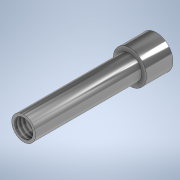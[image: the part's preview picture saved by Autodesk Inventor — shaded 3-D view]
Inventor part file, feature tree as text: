
AUTODESK INVENTOR PART (.ipt)
format: ipt  version: 2021 (Build 250183000, 183)  size: 116,736 bytes
history: native  units: mm
features: extrude x3, sketch x3, other x1, thread x1
ambient origin geometry x8: Origin, YZ Plane, XZ Plane, XY Plane, X Axis, Y Axis, Z Axis, Center Point
bodies: Body1 (feature_tree)
feature tree (8):
  other  "Sólido1"
  extrude  "Extrusão1"  Depth=10.0mm TaperAngle=0.0deg
  extrude  "Extrusão2"  Depth=2.0mm TaperAngle=0.0deg
  extrude  "Extrusão3"  Depth=8.0mm TaperAngle=0.0deg
  thread  "Rosca1"  [1 undecoded]
  sketch  "Esboço1"  dims[d0=1.8mm d1=10.0mm d2=0.0mm]
  sketch  "Esboço2"  dims[d3=2.5mm d4=2.0mm d5=0.0mm]
  sketch  "Esboço3"  dims[d6=1.4mm d7=8.0mm d8=0.0mm d9=8.0mm d10=0.0mm]
note: 1 required parameter value undecoded (feature->parameter linkage not recoverable at this tier; creation-order binding heuristic only, values carry confidence <= 0.55)
